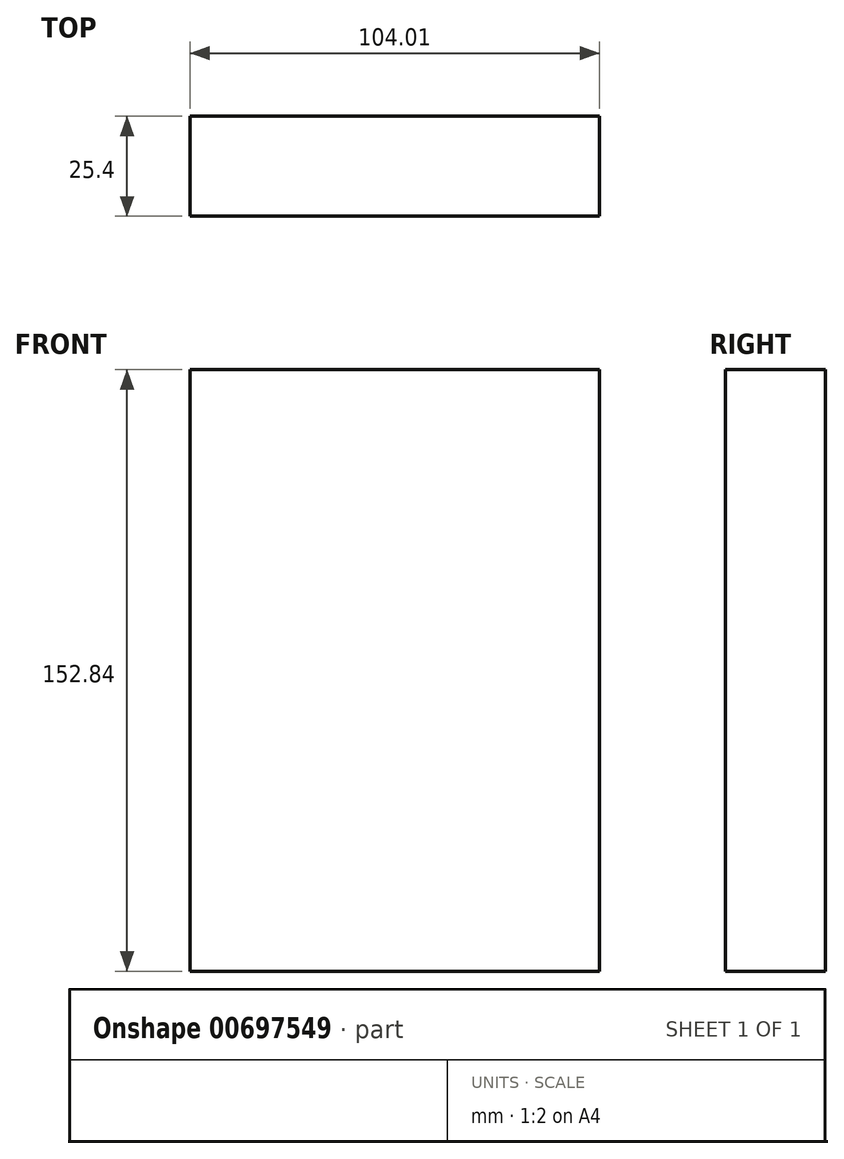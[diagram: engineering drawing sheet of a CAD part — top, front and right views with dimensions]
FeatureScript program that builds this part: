
annotation { "Feature Type Name" : "Feature", "Feature Type Description" : "" }
export const myFeature = defineFeature(function(context is Context, id is Id, definition is map)
    precondition{}
    {
        {
            var Q0;
            Q0=qCreatedBy(makeId("Front.planeOp"),FACE);
            var sketch = newSketch(context, id + "F0", { "sketchPlane" : qUnion([Q0])});
            skLineSegment(sketch, "E0.bottom", {"start": v(0, 111.81) * mm, "end": v(-104.01, 111.81) * mm});
            skLineSegment(sketch, "E0.top", {"start": v(0, -41.03) * mm, "end": v(-104.01, -41.03) * mm});
            skLineSegment(sketch, "E0.left", {"start": v(0, 111.81) * mm, "end": v(0, -41.03) * mm});
            skLineSegment(sketch, "E0.right", {"start": v(-104.01, 111.81) * mm, "end": v(-104.01, -41.03) * mm});
            skSolve(sketch);
        }
        {
            var Q0;
            Q0=sQuery(id+"F0.wireOp",EDGE,"E0.right");
            var Q1;
            Q1=sQuery(id+"F0.wireOp",EDGE,"E0.bottom");
            var Q2;
            Q2=sQuery(id+"F0.wireOp",EDGE,"E0.top");
            var Q3;
            Q3=sQuery(id+"F0.wireOp",EDGE,"E0.left");
            extrude(context, id + "F1", {"bodyType" : ToolBodyType.SURFACE, "surfaceEntities" : qUnion([Q0, Q1, Q2, Q3]), "depth" : 25.4 * mm, "offsetDistance" : 25.4 * mm});
        }
    });
